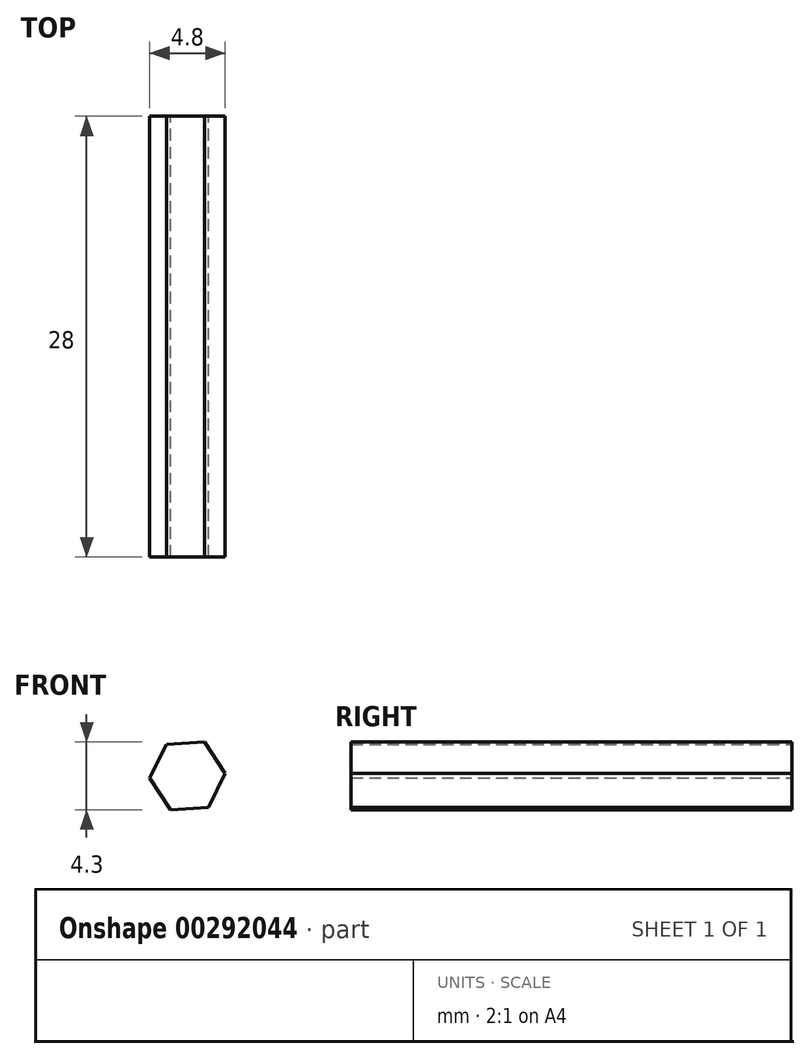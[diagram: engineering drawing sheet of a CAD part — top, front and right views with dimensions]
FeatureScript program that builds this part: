
annotation { "Feature Type Name" : "Feature", "Feature Type Description" : "" }
export const myFeature = defineFeature(function(context is Context, id is Id, definition is map)
    precondition{}
    {
        {
            var Q0;
            Q0=qCreatedBy(makeId("Front.planeOp"),FACE);
            var sketch = newSketch(context, id + "F0", { "sketchPlane" : qUnion([Q0])});
            skCircle(sketch, "E0.cCircle", {"center": v(0, 0) * mm, "radius": 2.08 * mm, "construction": true});
            skLineSegment(sketch, "E0.0", {"start": v(-2.4, -0.14) * mm, "end": v(-1.32, 2) * mm});
            skLineSegment(sketch, "E0.1", {"start": v(-1.32, 2) * mm, "end": v(1.07, 2.15) * mm});
            skLineSegment(sketch, "E0.2", {"start": v(1.07, 2.15) * mm, "end": v(2.4, 0.14) * mm});
            skLineSegment(sketch, "E0.3", {"start": v(2.4, 0.14) * mm, "end": v(1.32, -2) * mm});
            skLineSegment(sketch, "E0.4", {"start": v(1.32, -2) * mm, "end": v(-1.07, -2.15) * mm});
            skLineSegment(sketch, "E0.5", {"start": v(-1.07, -2.15) * mm, "end": v(-2.4, -0.14) * mm});
            skPoint(sketch, "E0.0.midPoint", {"position": v(-1.86, 0.93) * mm});
            skSolve(sketch);
        }
        {
            var Q0;
            Q0 = qSketchRegion(id + "F0", true);
            extrude(context, id + "F1", {"entities" : qUnion([Q0]), "depth" : 28 * mm});
        }
    });
